# Revit family: RN 84223 Optiflex-Flowpress-Modulo GIS
name_source: partatom
category: HLS-Bauteile
units: mm (PartAtom-declared; Revit-internal decimal feet)

## family parameters
Arbeitsebenenbasiert = Nein
Beim Laden mit Abzugskörper schneiden = Nein
Bemaßung runder Anschluss = Durchmesser verwenden
Gemeinsam genutzt = Nein
Immer vertikal = Ja
Klassifizierung = Keine
Raumberechnungspunkt = Nein
Teiletyp = Normal

## types (1)
- DN=15x12
    1.010.00.2 Blattnummer der Richtlinie = 29
    1.010.00.3 Ausgabedatum (Monat) der Richtlinie = 201308
    1.010.00.4 Herstellername = R. Nussbaum AG
    1.010.00.5 Revisionsdatum der Datei = 20190521
    1.010.00.6 Webadresse des Herstellers = http://www.nussbaum.ch
    1.100.00.4 Produktbezeichnung = Versorgung
    1.110.00.2 Index = 5
    1.110.00.4 Produktbezeichnung = Optiflex
    1.800.00.3 TGA-Nummer = 01900500000000000000000000000000000000000000000012000000000000000001
    1.800.00.4 Kommentarfeld = 84223.21, Optiflex-Flowpress-GIS-Modul, für Waschtisch, DN=15x12, L=153, Rp=½
    1.810.00.3 Hersteller-Bestellnummer = 84223.21
    1.810.00.4 DATANORM-Nummer = 84223.21
    1.810.00.5 StLB-Nummer = 322.621
    1.810.00.6 GTIN-Nummer = 7612945731753
    1.960/3L.00.8 Link (URL) = https://www.nussbaum.ch
    29.700.00.4 Produktname = Optiflex-Flowpress-GIS-Modul, für Waschtisch
    29.700.00.5 Produktkennung = 2
    29.700.00.6 Querschnittsform = 1
    29.700.00.7 Nennweitensystem = DN
    29.700.00.8 Nenndrucksystem = PN
    29.710.02.10 Formstück-Gewicht [kg] = 1.004
    29.710.02.3 Benennung = Optiflex-Flowpress-GIS-Modul, für Waschtisch, DN=15x12, L=153, Rp=½
    29.710.02.4 Nenndruck = 10
    29.710.02.5 max. zul. Überdruck [hPa] = 1000
    29.710.02.7 max. zul. Dauer-Betriebsdruck [hPa] = 1000
    29.710.02.9 max. zul. Dauer-Betriebstemperatur [°C] = 70
    CONNECTOR0_DIAMETER_dZ_0r = 12 mm  [stored 0.0393701 ft]
    CONNECTOR0_dZ_00 = 54 mm
    CONNECTOR0_dZ_01 = 40 mm
    CONNECTOR0_ref_dX = 77 mm
    CONNECTOR0_ref_dY = 21 mm
    CONNECTOR0_ref_dZ = 40 mm
    CONNECTOR1_DIAMETER_dZ_0r = 12 mm  [stored 0.0393701 ft]
    CONNECTOR1_dZ_00 = 54 mm
    CONNECTOR1_dZ_01 = 40 mm
    CONNECTOR1_ref_dX = 77 mm
    CONNECTOR1_ref_dY = 21 mm
    CONNECTOR1_ref_dZ = 40 mm
    CONNECTOR2_DIAMETER_dY_0r = 15 mm
    CONNECTOR2_dY_00 = 66 mm
    CONNECTOR2_dY_01 = 53 mm
    CONNECTOR2_ref_dX = 77 mm
    CONNECTOR2_ref_dY = 53 mm
    CONNECTOR3_DIAMETER_dY_0r = 15 mm
    CONNECTOR3_dY_00 = 66 mm
    CONNECTOR3_dY_01 = 53 mm
    CONNECTOR3_ref_dX = 77 mm
    CONNECTOR3_ref_dY = 53 mm
    Connector Visibility = Nein
    EnclosingSpace Visibility = Nein
    Hersteller = R. Nussbaum AG
    Modell = 84223.21
    R. Nussbaum AG 84223.21 de Visibility = Ja
    Typenkommentare = Optiflex-Flowpress-Modulo GIS DN=15x12
    URL = https://www.nussbaum.ch

note: [stored X ft] marks values corroborated as IEEE doubles in the binary element streams (Revit-internal decimal feet)

## geometry (parser evidence)
native form markers: Sweep x2
no freeform markers — native parametric forms only
